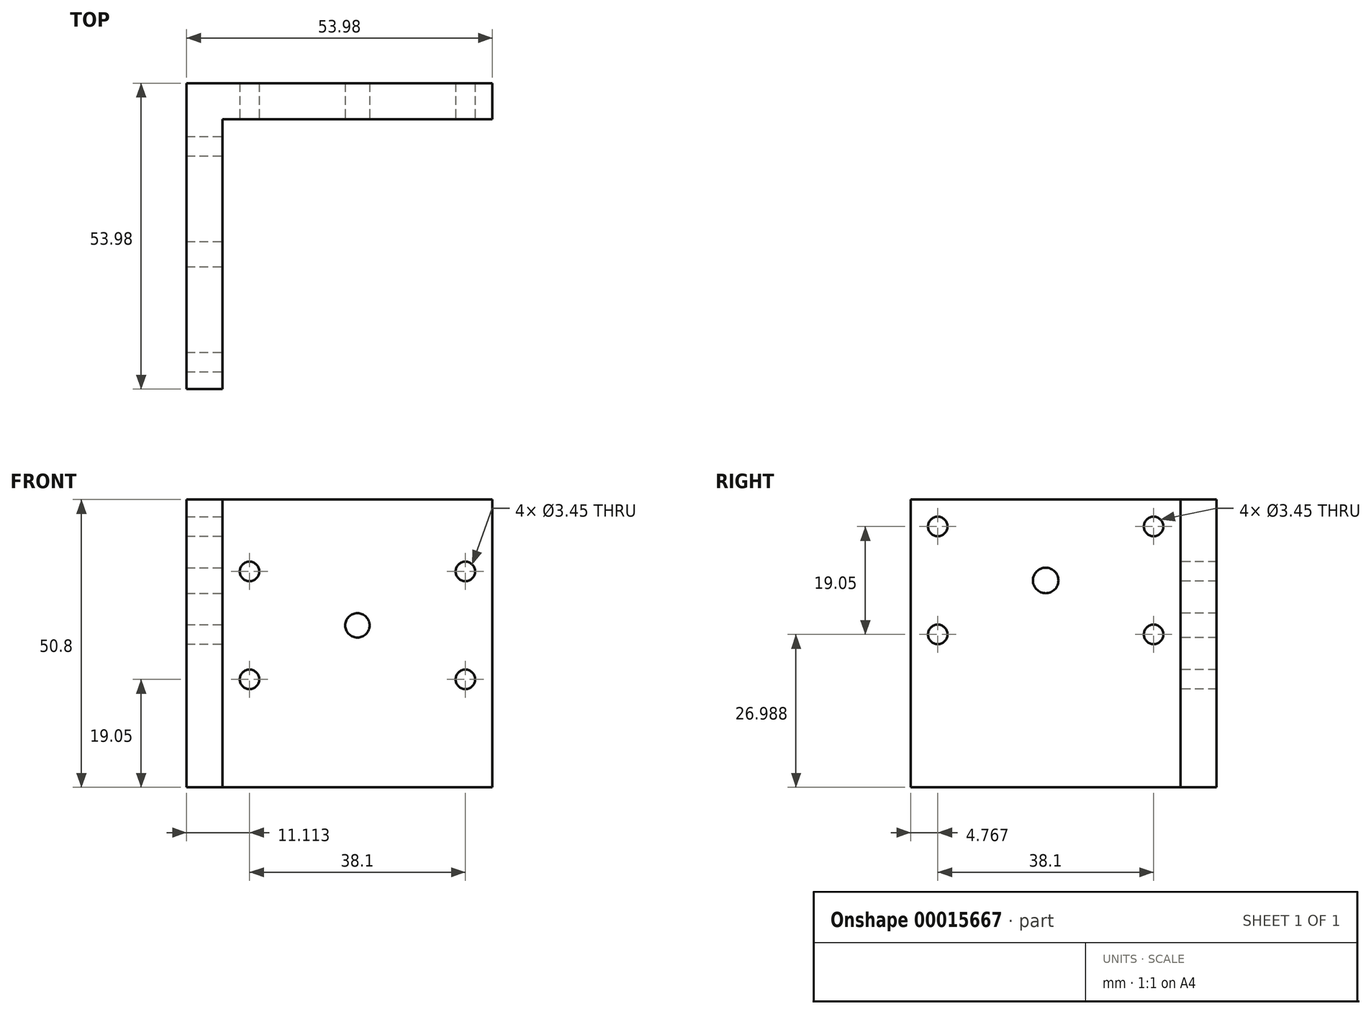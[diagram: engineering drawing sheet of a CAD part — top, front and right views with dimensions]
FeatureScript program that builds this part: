
annotation { "Feature Type Name" : "Feature", "Feature Type Description" : "" }
export const myFeature = defineFeature(function(context is Context, id is Id, definition is map)
    precondition{}
    {
        {
            var Q0;
            Q0=qCreatedBy(makeId("Top.planeOp"),FACE);
            var sketch = newSketch(context, id + "F0", { "sketchPlane" : qUnion([Q0])});
            skLineSegment(sketch, "E0.bottom", {"start": v(0, 0) * mm, "end": v(53.98, 0) * mm});
            skLineSegment(sketch, "E0.left", {"start": v(0, 0) * mm, "end": v(0, -53.98) * mm});
            skLineSegment(sketch, "E1.top", {"start": v(53.98, -6.35) * mm, "end": v(6.35, -6.35) * mm});
            skLineSegment(sketch, "E1.right", {"start": v(6.35, -53.98) * mm, "end": v(6.35, -6.35) * mm});
            skLineSegment(sketch, "E2", {"start": v(0, -53.98) * mm, "end": v(6.35, -53.98) * mm});
            skLineSegment(sketch, "E3", {"start": v(53.98, -6.35) * mm, "end": v(53.98, 0) * mm});
            skSolve(sketch);
        }
        {
            var Q0;
            Q0 = qSketchRegion(id + "F0", true);
            extrude(context, id + "F1", {"entities" : qUnion([Q0]), "depth" : 50.8 * mm});
        }
        {
            var Q0;
            Q0=makeQuery(id+"F1.opExtrude","SWEPT_FACE",FACE,{"disambiguationData":[OSD([sQuery(id+"F0.wireOp",EDGE,"E1.right")])]});
            var sketch = newSketch(context, id + "F2", { "sketchPlane" : qUnion([Q0])});
            skLineSegment(sketch, "E4.bottom", {"start": v(-49.21, 46.04) * mm, "end": v(-11.11, 46.04) * mm, "construction": true});
            skLineSegment(sketch, "E4.top", {"start": v(-49.21, 26.99) * mm, "end": v(-11.11, 26.99) * mm, "construction": true});
            skLineSegment(sketch, "E4.left", {"start": v(-49.21, 46.04) * mm, "end": v(-49.21, 26.99) * mm, "construction": true});
            skLineSegment(sketch, "E4.right", {"start": v(-11.11, 46.04) * mm, "end": v(-11.11, 26.99) * mm, "construction": true});
            skPoint(sketch, "E4.middle", {"position": v(-30.16, 36.51) * mm});
            skLineSegment(sketch, "E5.bottom", {"start": v(-49.21, 46.04) * mm, "end": v(-53.98, 46.04) * mm, "construction": true});
            skLineSegment(sketch, "E5.top", {"start": v(-49.21, 50.8) * mm, "end": v(-53.98, 50.8) * mm, "construction": true});
            skLineSegment(sketch, "E5.left", {"start": v(-49.21, 46.04) * mm, "end": v(-49.21, 50.8) * mm, "construction": true});
            skLineSegment(sketch, "E5.right", {"start": v(-53.98, 46.04) * mm, "end": v(-53.98, 50.8) * mm, "construction": true});
            skCircle(sketch, "E6", {"center": v(-11.11, 46.04) * mm, "radius": 1.73 * mm});
            skCircle(sketch, "E7", {"center": v(-11.11, 26.99) * mm, "radius": 1.73 * mm});
            skCircle(sketch, "E8", {"center": v(-49.21, 46.04) * mm, "radius": 1.73 * mm});
            skCircle(sketch, "E9", {"center": v(-30.16, 36.51) * mm, "radius": 2.25 * mm});
            skCircle(sketch, "E10", {"center": v(-49.21, 26.99) * mm, "radius": 1.73 * mm});
            skSolve(sketch);
        }
        {
            var Q0;
            Q0 = qSketchRegion(id + "F2", true);
            var Q1;
            Q1=makeQuery(id+"F1.opExtrude","SWEPT_FACE",FACE,{"disambiguationData":[OSD([sQuery(id+"F0.wireOp",EDGE,"E0.left")])]});
            extrude(context, id + "F3", {"entities" : qUnion([Q0]), "operationType" : NewBodyOperationType.REMOVE, "endBound" : BoundingType.UP_TO_SURFACE, "oppositeDirection" : true, "endBoundEntityFace" : qUnion([Q1]), "depth" : 25.4 * mm});
        }
        {
            var Q0;
            Q0=makeQuery(id+"F1.opExtrude","SWEPT_FACE",FACE,{"disambiguationData":[OSD([sQuery(id+"F0.wireOp",EDGE,"E1.top")])]});
            var sketch = newSketch(context, id + "F4", { "sketchPlane" : qUnion([Q0])});
            skLineSegment(sketch, "E11.bottom", {"start": v(49.21, 19.05) * mm, "end": v(11.11, 19.05) * mm, "construction": true});
            skLineSegment(sketch, "E11.top", {"start": v(49.21, 38.1) * mm, "end": v(11.11, 38.1) * mm, "construction": true});
            skLineSegment(sketch, "E11.left", {"start": v(49.21, 19.05) * mm, "end": v(49.21, 38.1) * mm, "construction": true});
            skLineSegment(sketch, "E11.right", {"start": v(11.11, 19.05) * mm, "end": v(11.11, 38.1) * mm, "construction": true});
            skPoint(sketch, "E11.middle", {"position": v(30.16, 28.57) * mm});
            skLineSegment(sketch, "E12.bottom", {"start": v(49.21, 38.1) * mm, "end": v(53.98, 38.1) * mm, "construction": true});
            skLineSegment(sketch, "E12.top", {"start": v(49.21, 50.8) * mm, "end": v(53.98, 50.8) * mm, "construction": true});
            skLineSegment(sketch, "E12.left", {"start": v(49.21, 50.8) * mm, "end": v(49.21, 38.1) * mm, "construction": true});
            skLineSegment(sketch, "E12.right", {"start": v(53.98, 50.8) * mm, "end": v(53.98, 38.1) * mm, "construction": true});
            skCircle(sketch, "E13", {"center": v(30.16, 28.57) * mm, "radius": 2.15 * mm});
            skCircle(sketch, "E14", {"center": v(49.21, 38.1) * mm, "radius": 1.73 * mm});
            skCircle(sketch, "E15", {"center": v(49.21, 19.05) * mm, "radius": 1.73 * mm});
            skCircle(sketch, "E16", {"center": v(11.11, 19.05) * mm, "radius": 1.73 * mm});
            skCircle(sketch, "E17", {"center": v(11.11, 38.1) * mm, "radius": 1.73 * mm});
            skSolve(sketch);
        }
        {
            var Q0;
            Q0 = qSketchRegion(id + "F4", true);
            var Q1;
            Q1=makeQuery(id+"F1.opExtrude","SWEPT_FACE",FACE,{"disambiguationData":[OSD([sQuery(id+"F0.wireOp",EDGE,"E0.bottom")])]});
            extrude(context, id + "F5", {"entities" : qUnion([Q0]), "operationType" : NewBodyOperationType.REMOVE, "endBound" : BoundingType.UP_TO_SURFACE, "oppositeDirection" : true, "endBoundEntityFace" : qUnion([Q1]), "depth" : 25.4 * mm});
        }
    });
